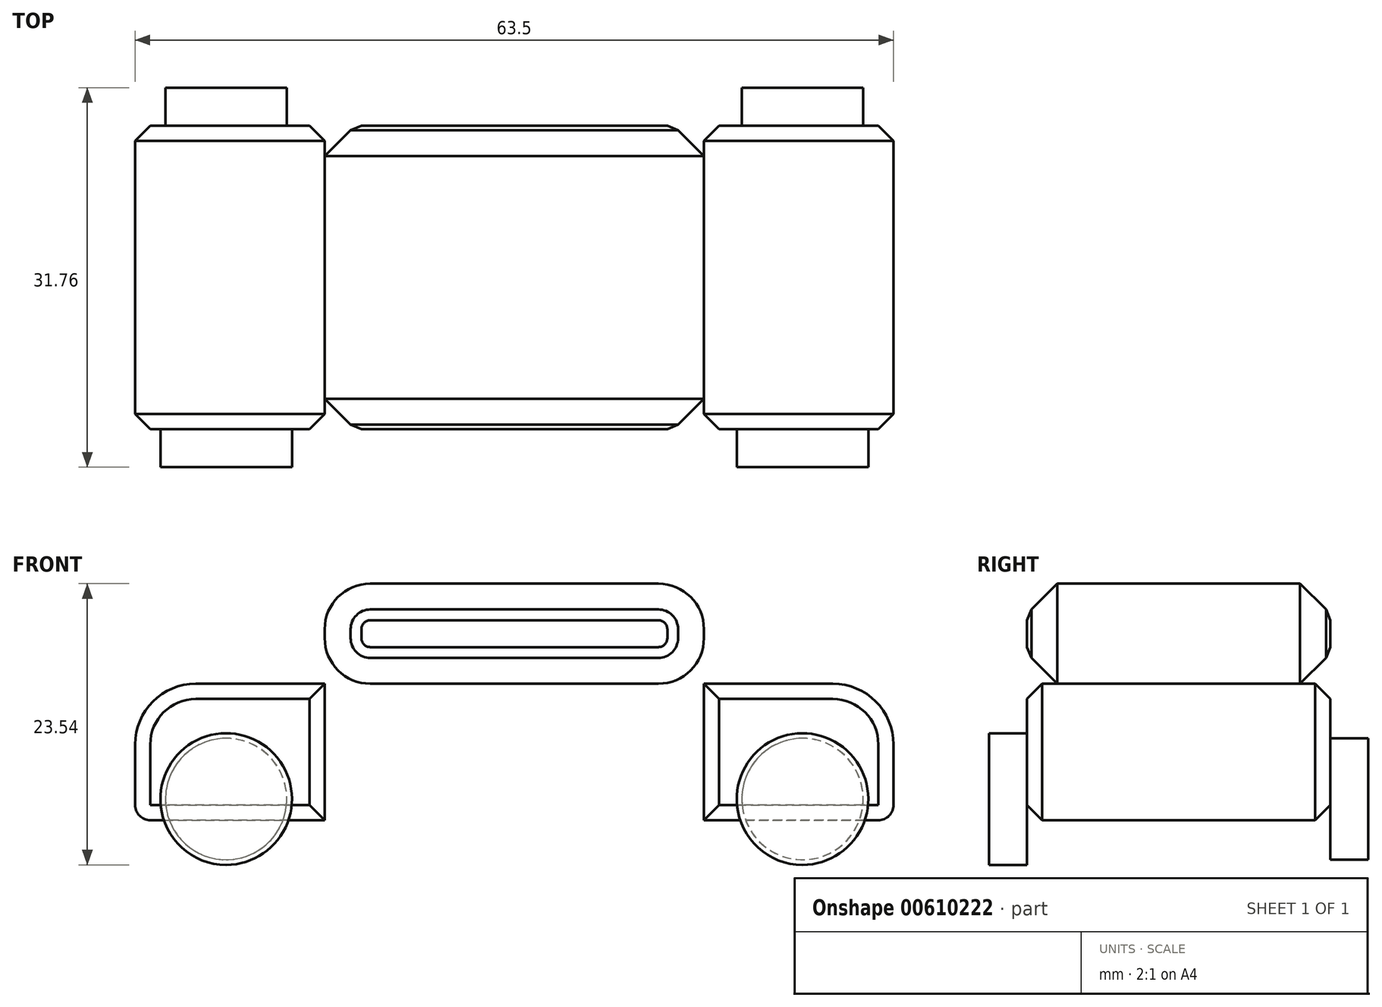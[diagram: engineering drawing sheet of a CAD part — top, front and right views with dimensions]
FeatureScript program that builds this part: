
annotation { "Feature Type Name" : "Feature", "Feature Type Description" : "" }
export const myFeature = defineFeature(function(context is Context, id is Id, definition is map)
    precondition{}
    {
        {
            var Q0;
            Q0=qCreatedBy(makeId("Top.planeOp"),FACE);
            var sketch = newSketch(context, id + "F0", { "sketchPlane" : qUnion([Q0])});
            skLineSegment(sketch, "E0.bottom", {"start": v(0, 0) * mm, "end": v(63.5, 0) * mm});
            skLineSegment(sketch, "E0.top", {"start": v(0, 25.4) * mm, "end": v(63.5, 25.4) * mm});
            skLineSegment(sketch, "E0.left", {"start": v(0, 0) * mm, "end": v(0, 25.4) * mm});
            skLineSegment(sketch, "E0.right", {"start": v(63.5, 0) * mm, "end": v(63.5, 25.4) * mm});
            skLineSegment(sketch, "E1.bottom", {"start": v(47.62, 0) * mm, "end": v(15.88, 0) * mm});
            skLineSegment(sketch, "E1.top", {"start": v(47.62, 25.4) * mm, "end": v(15.88, 25.4) * mm});
            skLineSegment(sketch, "E1.left", {"start": v(47.62, 0) * mm, "end": v(47.62, 25.4) * mm});
            skLineSegment(sketch, "E1.right", {"start": v(15.88, 0) * mm, "end": v(15.88, 25.4) * mm});
            skPoint(sketch, "E1.middle", {"position": v(31.75, 12.7) * mm});
            skSolve(sketch);
        }
        {
            var Q0;
            Q0=makeQuery(id+"F0.imprint","IMPRINT",FACE,{"disambiguationData":[TD([[makeQuery(id+"F0.imprint","IMPRINT",EDGE,{"derivedFrom":sQuery(id+"F0.wireOp",EDGE,"E1.bottom")}),-1.0]])]});
            var Q1;
            {var subQ0=sQuery(id+"F0.wireOp",EDGE,"E0.left");Q1=makeQuery(id+"F0.imprint","IMPRINT",FACE,{"disambiguationData":[TD([[makeQuery(id+"F0.imprint","IMPRINT",EDGE,{"derivedFrom":subQ0}),-1.0]])]});}
            var Q2;
            {var subQ0=sQuery(id+"F0.wireOp",EDGE,"E0.right");Q2=makeQuery(id+"F0.imprint","IMPRINT",FACE,{"disambiguationData":[TD([[makeQuery(id+"F0.imprint","IMPRINT",EDGE,{"derivedFrom":subQ0}),1.0]])]});}
            extrude(context, id + "F1", {"entities" : qUnion([Q0, Q1, Q2]), "depth" : 11.43 * mm, "offsetDistance" : 25.4 * mm});
        }
        {
            var Q0;
            Q0=makeQuery(id+"F1.opExtrude","CAP_FACE",FACE,{"disambiguationData":[OSD([sQuery(id+"F0.wireOp",EDGE,"E0.bottom"),sQuery(id+"F0.wireOp",EDGE,"E0.top"),sQuery(id+"F0.wireOp",EDGE,"E0.left"),sQuery(id+"F0.wireOp",EDGE,"E0.right"),sQuery(id+"F0.wireOp",EDGE,"E1.bottom"),sQuery(id+"F0.wireOp",EDGE,"E1.top")])],"isStart":false});
            var sketch = newSketch(context, id + "F2", { "sketchPlane" : qUnion([Q0])});
            skLineSegment(sketch, "E2.bottom", {"start": v(47.62, 0) * mm, "end": v(15.88, 0) * mm});
            skLineSegment(sketch, "E2.top", {"start": v(47.62, 25.4) * mm, "end": v(15.88, 25.4) * mm});
            skLineSegment(sketch, "E2.left", {"start": v(47.62, 0) * mm, "end": v(47.62, 25.4) * mm});
            skLineSegment(sketch, "E2.right", {"start": v(15.88, 0) * mm, "end": v(15.88, 25.4) * mm});
            skSolve(sketch);
        }
        {
            var Q0;
            Q0 = qSketchRegion(id + "F2", true);
            extrude(context, id + "F3", {"entities" : qUnion([Q0]), "operationType" : NewBodyOperationType.ADD, "depth" : 8.38 * mm, "offsetDistance" : 25.4 * mm});
        }
        {
            var Q0;
            Q0=makeQuery(id+"F3.opExtrude","CAP_EDGE",EDGE,{"disambiguationData":[OSD([sQuery(id+"F2.wireOp",EDGE,"E2.right")])],"isStart":true});
            var Q1;
            Q1=makeQuery(id+"F3.opExtrude","CAP_EDGE",EDGE,{"disambiguationData":[OSD([sQuery(id+"F2.wireOp",EDGE,"E2.left")])],"isStart":true});
            var Q2;
            Q2=makeQuery(id+"F3.opExtrude","CAP_EDGE",EDGE,{"disambiguationData":[OSD([sQuery(id+"F2.wireOp",EDGE,"E2.left")])],"isStart":false});
            var Q3;
            Q3=makeQuery(id+"F3.opExtrude","CAP_EDGE",EDGE,{"disambiguationData":[OSD([sQuery(id+"F2.wireOp",EDGE,"E2.right")])],"isStart":false});
            fillet(context, id + "F4", {"entities" : qUnion([Q0, Q1, Q2, Q3]), "radius" : 3.8 * mm, "tangentPropagation" : true, "allowEdgeOverflow" : false});
        }
        {
            var Q0;
            Q0=makeQuery(id+"F1.opExtrude","CAP_EDGE",EDGE,{"disambiguationData":[OSD([sQuery(id+"F0.wireOp",EDGE,"E0.right")])],"isStart":false});
            var Q1;
            Q1=makeQuery(id+"F1.opExtrude","CAP_EDGE",EDGE,{"disambiguationData":[OSD([sQuery(id+"F0.wireOp",EDGE,"E0.left")])],"isStart":false});
            fillet(context, id + "F5", {"entities" : qUnion([Q0, Q1]), "radius" : 5.08 * mm, "tangentPropagation" : true, "allowEdgeOverflow" : false});
        }
        {
            var Q0;
            Q0=makeQuery(id+"F1.opExtrude","CAP_EDGE",EDGE,{"disambiguationData":[OSD([sQuery(id+"F0.wireOp",EDGE,"E0.right")])],"isStart":true});
            var Q1;
            Q1=makeQuery(id+"F1.opExtrude","CAP_EDGE",EDGE,{"disambiguationData":[OSD([sQuery(id+"F0.wireOp",EDGE,"E0.left")])],"isStart":true});
            fillet(context, id + "F6", {"entities" : qUnion([Q0, Q1]), "radius" : 1.27 * mm, "tangentPropagation" : true, "allowEdgeOverflow" : false});
        }
        {
            var Q0;
            Q0=makeQuery(id+"F5.opFillet","BLEND_EDGE",EDGE,{"blendedFrom":[makeQuery(id+"F1.opExtrude","CAP_EDGE",EDGE,{"disambiguationData":[OSD([sQuery(id+"F0.wireOp",EDGE,"E0.right")])],"isStart":false}),makeQuery(id+"F3.boolean.opBoolean","MERGE",FACE,{"derivedFrom":[makeQuery(id+"F1.opExtrude","SWEPT_FACE",FACE,{"disambiguationData":[OSD([sQuery(id+"F0.wireOp",EDGE,"E0.top"),sQuery(id+"F0.wireOp",EDGE,"E1.top")])]}),makeQuery(id+"F3.opExtrude","SWEPT_FACE",FACE,{"disambiguationData":[OSD([sQuery(id+"F2.wireOp",EDGE,"E2.top")])]})]})],"blendedInto":[makeQuery(id+"F3.boolean.opBoolean","MERGE",FACE,{"derivedFrom":[makeQuery(id+"F1.opExtrude","SWEPT_FACE",FACE,{"disambiguationData":[OSD([sQuery(id+"F0.wireOp",EDGE,"E0.top"),sQuery(id+"F0.wireOp",EDGE,"E1.top")])]}),makeQuery(id+"F3.opExtrude","SWEPT_FACE",FACE,{"disambiguationData":[OSD([sQuery(id+"F2.wireOp",EDGE,"E2.top")])]})]})]});
            var Q1;
            Q1=makeQuery(id+"F1.opExtrude","SWEPT_EDGE",EDGE,{"disambiguationData":[OSD([sQuery(id+"F0.wireOp",EDGE,"E0.top"),sQuery(id+"F0.wireOp",EDGE,"E0.right")])]});
            var Q2;
            Q2=makeQuery(id+"F6.opFillet","BLEND_EDGE",EDGE,{"blendedFrom":[makeQuery(id+"F1.opExtrude","CAP_EDGE",EDGE,{"disambiguationData":[OSD([sQuery(id+"F0.wireOp",EDGE,"E0.right")])],"isStart":true}),makeQuery(id+"F3.boolean.opBoolean","MERGE",FACE,{"derivedFrom":[makeQuery(id+"F1.opExtrude","SWEPT_FACE",FACE,{"disambiguationData":[OSD([sQuery(id+"F0.wireOp",EDGE,"E0.top"),sQuery(id+"F0.wireOp",EDGE,"E1.top")])]}),makeQuery(id+"F3.opExtrude","SWEPT_FACE",FACE,{"disambiguationData":[OSD([sQuery(id+"F2.wireOp",EDGE,"E2.top")])]})]})],"blendedInto":[makeQuery(id+"F3.boolean.opBoolean","MERGE",FACE,{"derivedFrom":[makeQuery(id+"F1.opExtrude","SWEPT_FACE",FACE,{"disambiguationData":[OSD([sQuery(id+"F0.wireOp",EDGE,"E0.top"),sQuery(id+"F0.wireOp",EDGE,"E1.top")])]}),makeQuery(id+"F3.opExtrude","SWEPT_FACE",FACE,{"disambiguationData":[OSD([sQuery(id+"F2.wireOp",EDGE,"E2.top")])]})]})]});
            var Q3;
            Q3=makeQuery(id+"F1.opExtrude","CAP_EDGE",EDGE,{"disambiguationData":[OSD([sQuery(id+"F0.wireOp",EDGE,"E0.top"),sQuery(id+"F0.wireOp",EDGE,"E1.top")])],"isStart":true});
            var Q4;
            {var subQ0=sQuery(id+"F0.wireOp",EDGE,"E0.right");var subQ1=sQuery(id+"F0.wireOp",EDGE,"E1.top");var subQ2=sQuery(id+"F0.wireOp",EDGE,"E0.top");Q4=makeQuery(id+"F3.boolean.opBoolean","SPLIT",EDGE,{"disambiguationData":[TD([makeQuery(id+"F1.opExtrude","SWEPT_FACE",FACE,{"disambiguationData":[OSD([subQ0])]})])],"derivedFrom":makeQuery(id+"F1.opExtrude","CAP_EDGE",EDGE,{"disambiguationData":[OSD([subQ2,subQ1])],"isStart":false})});}
            var Q5;
            Q5=makeQuery(id+"F4.opFillet","BLEND_EDGE",EDGE,{"blendedFrom":[makeQuery(id+"F3.opExtrude","CAP_EDGE",EDGE,{"disambiguationData":[OSD([sQuery(id+"F2.wireOp",EDGE,"E2.left")])],"isStart":true}),makeQuery(id+"F3.boolean.opBoolean","MERGE",FACE,{"derivedFrom":[makeQuery(id+"F1.opExtrude","SWEPT_FACE",FACE,{"disambiguationData":[OSD([sQuery(id+"F0.wireOp",EDGE,"E0.top"),sQuery(id+"F0.wireOp",EDGE,"E1.top")])]}),makeQuery(id+"F3.opExtrude","SWEPT_FACE",FACE,{"disambiguationData":[OSD([sQuery(id+"F2.wireOp",EDGE,"E2.top")])]})]})],"blendedInto":[makeQuery(id+"F3.boolean.opBoolean","MERGE",FACE,{"derivedFrom":[makeQuery(id+"F1.opExtrude","SWEPT_FACE",FACE,{"disambiguationData":[OSD([sQuery(id+"F0.wireOp",EDGE,"E0.top"),sQuery(id+"F0.wireOp",EDGE,"E1.top")])]}),makeQuery(id+"F3.opExtrude","SWEPT_FACE",FACE,{"disambiguationData":[OSD([sQuery(id+"F2.wireOp",EDGE,"E2.top")])]})]})]});
            var Q6;
            Q6=makeQuery(id+"F4.opFillet","BLEND_EDGE",EDGE,{"blendedFrom":[makeQuery(id+"F3.opExtrude","CAP_EDGE",EDGE,{"disambiguationData":[OSD([sQuery(id+"F2.wireOp",EDGE,"E2.left")])],"isStart":false}),makeQuery(id+"F3.boolean.opBoolean","MERGE",FACE,{"derivedFrom":[makeQuery(id+"F1.opExtrude","SWEPT_FACE",FACE,{"disambiguationData":[OSD([sQuery(id+"F0.wireOp",EDGE,"E0.top"),sQuery(id+"F0.wireOp",EDGE,"E1.top")])]}),makeQuery(id+"F3.opExtrude","SWEPT_FACE",FACE,{"disambiguationData":[OSD([sQuery(id+"F2.wireOp",EDGE,"E2.top")])]})]})],"blendedInto":[makeQuery(id+"F3.boolean.opBoolean","MERGE",FACE,{"derivedFrom":[makeQuery(id+"F1.opExtrude","SWEPT_FACE",FACE,{"disambiguationData":[OSD([sQuery(id+"F0.wireOp",EDGE,"E0.top"),sQuery(id+"F0.wireOp",EDGE,"E1.top")])]}),makeQuery(id+"F3.opExtrude","SWEPT_FACE",FACE,{"disambiguationData":[OSD([sQuery(id+"F2.wireOp",EDGE,"E2.top")])]})]})]});
            var Q7;
            Q7=makeQuery(id+"F3.opExtrude","CAP_EDGE",EDGE,{"disambiguationData":[OSD([sQuery(id+"F2.wireOp",EDGE,"E2.top")])],"isStart":false});
            var Q8;
            Q8=makeQuery(id+"F4.opFillet","BLEND_EDGE",EDGE,{"blendedFrom":[makeQuery(id+"F3.opExtrude","CAP_EDGE",EDGE,{"disambiguationData":[OSD([sQuery(id+"F2.wireOp",EDGE,"E2.right")])],"isStart":false}),makeQuery(id+"F3.boolean.opBoolean","MERGE",FACE,{"derivedFrom":[makeQuery(id+"F1.opExtrude","SWEPT_FACE",FACE,{"disambiguationData":[OSD([sQuery(id+"F0.wireOp",EDGE,"E0.top"),sQuery(id+"F0.wireOp",EDGE,"E1.top")])]}),makeQuery(id+"F3.opExtrude","SWEPT_FACE",FACE,{"disambiguationData":[OSD([sQuery(id+"F2.wireOp",EDGE,"E2.top")])]})]})],"blendedInto":[makeQuery(id+"F3.boolean.opBoolean","MERGE",FACE,{"derivedFrom":[makeQuery(id+"F1.opExtrude","SWEPT_FACE",FACE,{"disambiguationData":[OSD([sQuery(id+"F0.wireOp",EDGE,"E0.top"),sQuery(id+"F0.wireOp",EDGE,"E1.top")])]}),makeQuery(id+"F3.opExtrude","SWEPT_FACE",FACE,{"disambiguationData":[OSD([sQuery(id+"F2.wireOp",EDGE,"E2.top")])]})]})]});
            var Q9;
            Q9=makeQuery(id+"F4.opFillet","BLEND_EDGE",EDGE,{"blendedFrom":[makeQuery(id+"F3.opExtrude","CAP_EDGE",EDGE,{"disambiguationData":[OSD([sQuery(id+"F2.wireOp",EDGE,"E2.right")])],"isStart":true}),makeQuery(id+"F3.boolean.opBoolean","MERGE",FACE,{"derivedFrom":[makeQuery(id+"F1.opExtrude","SWEPT_FACE",FACE,{"disambiguationData":[OSD([sQuery(id+"F0.wireOp",EDGE,"E0.top"),sQuery(id+"F0.wireOp",EDGE,"E1.top")])]}),makeQuery(id+"F3.opExtrude","SWEPT_FACE",FACE,{"disambiguationData":[OSD([sQuery(id+"F2.wireOp",EDGE,"E2.top")])]})]})],"blendedInto":[makeQuery(id+"F3.boolean.opBoolean","MERGE",FACE,{"derivedFrom":[makeQuery(id+"F1.opExtrude","SWEPT_FACE",FACE,{"disambiguationData":[OSD([sQuery(id+"F0.wireOp",EDGE,"E0.top"),sQuery(id+"F0.wireOp",EDGE,"E1.top")])]}),makeQuery(id+"F3.opExtrude","SWEPT_FACE",FACE,{"disambiguationData":[OSD([sQuery(id+"F2.wireOp",EDGE,"E2.top")])]})]})]});
            var Q10;
            {var subQ0=sQuery(id+"F0.wireOp",EDGE,"E0.left");var subQ1=sQuery(id+"F0.wireOp",EDGE,"E1.top");var subQ2=sQuery(id+"F0.wireOp",EDGE,"E0.top");Q10=makeQuery(id+"F3.boolean.opBoolean","SPLIT",EDGE,{"disambiguationData":[TD([makeQuery(id+"F1.opExtrude","SWEPT_FACE",FACE,{"disambiguationData":[OSD([subQ0])]})])],"derivedFrom":makeQuery(id+"F1.opExtrude","CAP_EDGE",EDGE,{"disambiguationData":[OSD([subQ2,subQ1])],"isStart":false})});}
            var Q11;
            Q11=makeQuery(id+"F5.opFillet","BLEND_EDGE",EDGE,{"blendedFrom":[makeQuery(id+"F1.opExtrude","CAP_EDGE",EDGE,{"disambiguationData":[OSD([sQuery(id+"F0.wireOp",EDGE,"E0.left")])],"isStart":false}),makeQuery(id+"F3.boolean.opBoolean","MERGE",FACE,{"derivedFrom":[makeQuery(id+"F1.opExtrude","SWEPT_FACE",FACE,{"disambiguationData":[OSD([sQuery(id+"F0.wireOp",EDGE,"E0.top"),sQuery(id+"F0.wireOp",EDGE,"E1.top")])]}),makeQuery(id+"F3.opExtrude","SWEPT_FACE",FACE,{"disambiguationData":[OSD([sQuery(id+"F2.wireOp",EDGE,"E2.top")])]})]})],"blendedInto":[makeQuery(id+"F3.boolean.opBoolean","MERGE",FACE,{"derivedFrom":[makeQuery(id+"F1.opExtrude","SWEPT_FACE",FACE,{"disambiguationData":[OSD([sQuery(id+"F0.wireOp",EDGE,"E0.top"),sQuery(id+"F0.wireOp",EDGE,"E1.top")])]}),makeQuery(id+"F3.opExtrude","SWEPT_FACE",FACE,{"disambiguationData":[OSD([sQuery(id+"F2.wireOp",EDGE,"E2.top")])]})]})]});
            var Q12;
            Q12=makeQuery(id+"F1.opExtrude","SWEPT_EDGE",EDGE,{"disambiguationData":[OSD([sQuery(id+"F0.wireOp",EDGE,"E0.top"),sQuery(id+"F0.wireOp",EDGE,"E0.left")])]});
            var Q13;
            Q13=makeQuery(id+"F6.opFillet","BLEND_EDGE",EDGE,{"blendedFrom":[makeQuery(id+"F1.opExtrude","CAP_EDGE",EDGE,{"disambiguationData":[OSD([sQuery(id+"F0.wireOp",EDGE,"E0.left")])],"isStart":true}),makeQuery(id+"F3.boolean.opBoolean","MERGE",FACE,{"derivedFrom":[makeQuery(id+"F1.opExtrude","SWEPT_FACE",FACE,{"disambiguationData":[OSD([sQuery(id+"F0.wireOp",EDGE,"E0.top"),sQuery(id+"F0.wireOp",EDGE,"E1.top")])]}),makeQuery(id+"F3.opExtrude","SWEPT_FACE",FACE,{"disambiguationData":[OSD([sQuery(id+"F2.wireOp",EDGE,"E2.top")])]})]})],"blendedInto":[makeQuery(id+"F3.boolean.opBoolean","MERGE",FACE,{"derivedFrom":[makeQuery(id+"F1.opExtrude","SWEPT_FACE",FACE,{"disambiguationData":[OSD([sQuery(id+"F0.wireOp",EDGE,"E0.top"),sQuery(id+"F0.wireOp",EDGE,"E1.top")])]}),makeQuery(id+"F3.opExtrude","SWEPT_FACE",FACE,{"disambiguationData":[OSD([sQuery(id+"F2.wireOp",EDGE,"E2.top")])]})]})]});
            var Q14;
            Q14=makeQuery(id+"F1.opExtrude","CAP_EDGE",EDGE,{"disambiguationData":[OSD([sQuery(id+"F0.wireOp",EDGE,"E0.bottom"),sQuery(id+"F0.wireOp",EDGE,"E1.bottom")])],"isStart":true});
            var Q15;
            Q15=makeQuery(id+"F1.opExtrude","SWEPT_EDGE",EDGE,{"disambiguationData":[OSD([sQuery(id+"F0.wireOp",EDGE,"E0.bottom"),sQuery(id+"F0.wireOp",EDGE,"E0.left")])]});
            var Q16;
            Q16=makeQuery(id+"F5.opFillet","BLEND_EDGE",EDGE,{"blendedFrom":[makeQuery(id+"F1.opExtrude","CAP_EDGE",EDGE,{"disambiguationData":[OSD([sQuery(id+"F0.wireOp",EDGE,"E0.left")])],"isStart":false}),makeQuery(id+"F3.boolean.opBoolean","MERGE",FACE,{"derivedFrom":[makeQuery(id+"F1.opExtrude","SWEPT_FACE",FACE,{"disambiguationData":[OSD([sQuery(id+"F0.wireOp",EDGE,"E0.bottom"),sQuery(id+"F0.wireOp",EDGE,"E1.bottom")])]}),makeQuery(id+"F3.opExtrude","SWEPT_FACE",FACE,{"disambiguationData":[OSD([sQuery(id+"F2.wireOp",EDGE,"E2.bottom")])]})]})],"blendedInto":[makeQuery(id+"F3.boolean.opBoolean","MERGE",FACE,{"derivedFrom":[makeQuery(id+"F1.opExtrude","SWEPT_FACE",FACE,{"disambiguationData":[OSD([sQuery(id+"F0.wireOp",EDGE,"E0.bottom"),sQuery(id+"F0.wireOp",EDGE,"E1.bottom")])]}),makeQuery(id+"F3.opExtrude","SWEPT_FACE",FACE,{"disambiguationData":[OSD([sQuery(id+"F2.wireOp",EDGE,"E2.bottom")])]})]})]});
            var Q17;
            {var subQ0=sQuery(id+"F0.wireOp",EDGE,"E1.bottom");var subQ1=sQuery(id+"F0.wireOp",EDGE,"E0.left");var subQ2=sQuery(id+"F0.wireOp",EDGE,"E0.bottom");Q17=makeQuery(id+"F3.boolean.opBoolean","SPLIT",EDGE,{"disambiguationData":[TD([makeQuery(id+"F1.opExtrude","SWEPT_FACE",FACE,{"disambiguationData":[OSD([subQ1])]})])],"derivedFrom":makeQuery(id+"F1.opExtrude","CAP_EDGE",EDGE,{"disambiguationData":[OSD([subQ2,subQ0])],"isStart":false})});}
            var Q18;
            Q18=makeQuery(id+"F4.opFillet","BLEND_EDGE",EDGE,{"blendedFrom":[makeQuery(id+"F3.opExtrude","CAP_EDGE",EDGE,{"disambiguationData":[OSD([sQuery(id+"F2.wireOp",EDGE,"E2.right")])],"isStart":true}),makeQuery(id+"F3.boolean.opBoolean","MERGE",FACE,{"derivedFrom":[makeQuery(id+"F1.opExtrude","SWEPT_FACE",FACE,{"disambiguationData":[OSD([sQuery(id+"F0.wireOp",EDGE,"E0.bottom"),sQuery(id+"F0.wireOp",EDGE,"E1.bottom")])]}),makeQuery(id+"F3.opExtrude","SWEPT_FACE",FACE,{"disambiguationData":[OSD([sQuery(id+"F2.wireOp",EDGE,"E2.bottom")])]})]})],"blendedInto":[makeQuery(id+"F3.boolean.opBoolean","MERGE",FACE,{"derivedFrom":[makeQuery(id+"F1.opExtrude","SWEPT_FACE",FACE,{"disambiguationData":[OSD([sQuery(id+"F0.wireOp",EDGE,"E0.bottom"),sQuery(id+"F0.wireOp",EDGE,"E1.bottom")])]}),makeQuery(id+"F3.opExtrude","SWEPT_FACE",FACE,{"disambiguationData":[OSD([sQuery(id+"F2.wireOp",EDGE,"E2.bottom")])]})]})]});
            var Q19;
            Q19=makeQuery(id+"F4.opFillet","BLEND_EDGE",EDGE,{"blendedFrom":[makeQuery(id+"F3.opExtrude","CAP_EDGE",EDGE,{"disambiguationData":[OSD([sQuery(id+"F2.wireOp",EDGE,"E2.right")])],"isStart":false}),makeQuery(id+"F3.boolean.opBoolean","MERGE",FACE,{"derivedFrom":[makeQuery(id+"F1.opExtrude","SWEPT_FACE",FACE,{"disambiguationData":[OSD([sQuery(id+"F0.wireOp",EDGE,"E0.bottom"),sQuery(id+"F0.wireOp",EDGE,"E1.bottom")])]}),makeQuery(id+"F3.opExtrude","SWEPT_FACE",FACE,{"disambiguationData":[OSD([sQuery(id+"F2.wireOp",EDGE,"E2.bottom")])]})]})],"blendedInto":[makeQuery(id+"F3.boolean.opBoolean","MERGE",FACE,{"derivedFrom":[makeQuery(id+"F1.opExtrude","SWEPT_FACE",FACE,{"disambiguationData":[OSD([sQuery(id+"F0.wireOp",EDGE,"E0.bottom"),sQuery(id+"F0.wireOp",EDGE,"E1.bottom")])]}),makeQuery(id+"F3.opExtrude","SWEPT_FACE",FACE,{"disambiguationData":[OSD([sQuery(id+"F2.wireOp",EDGE,"E2.bottom")])]})]})]});
            var Q20;
            Q20=makeQuery(id+"F3.opExtrude","CAP_EDGE",EDGE,{"disambiguationData":[OSD([sQuery(id+"F2.wireOp",EDGE,"E2.bottom")])],"isStart":false});
            var Q21;
            Q21=makeQuery(id+"F3.opExtrude","SWEPT_EDGE",EDGE,{"disambiguationData":[OSD([sQuery(id+"F0.wireOp",EDGE,"E0.bottom"),sQuery(id+"F0.wireOp",EDGE,"E1.bottom"),sQuery(id+"F2.wireOp",EDGE,"E2.bottom"),sQuery(id+"F2.wireOp",EDGE,"E2.right")])]});
            var Q22;
            Q22=makeQuery(id+"F3.opExtrude","SWEPT_EDGE",EDGE,{"disambiguationData":[OSD([sQuery(id+"F0.wireOp",EDGE,"E0.top"),sQuery(id+"F0.wireOp",EDGE,"E1.top"),sQuery(id+"F2.wireOp",EDGE,"E2.top"),sQuery(id+"F2.wireOp",EDGE,"E2.right")])]});
            var Q23;
            Q23=makeQuery(id+"F1.opExtrude","SWEPT_EDGE",EDGE,{"disambiguationData":[OSD([sQuery(id+"F0.wireOp",EDGE,"E0.bottom"),sQuery(id+"F0.wireOp",EDGE,"E0.right")])]});
            var Q24;
            Q24=makeQuery(id+"F5.opFillet","BLEND_EDGE",EDGE,{"blendedFrom":[makeQuery(id+"F1.opExtrude","CAP_EDGE",EDGE,{"disambiguationData":[OSD([sQuery(id+"F0.wireOp",EDGE,"E0.right")])],"isStart":false}),makeQuery(id+"F3.boolean.opBoolean","MERGE",FACE,{"derivedFrom":[makeQuery(id+"F1.opExtrude","SWEPT_FACE",FACE,{"disambiguationData":[OSD([sQuery(id+"F0.wireOp",EDGE,"E0.bottom"),sQuery(id+"F0.wireOp",EDGE,"E1.bottom")])]}),makeQuery(id+"F3.opExtrude","SWEPT_FACE",FACE,{"disambiguationData":[OSD([sQuery(id+"F2.wireOp",EDGE,"E2.bottom")])]})]})],"blendedInto":[makeQuery(id+"F3.boolean.opBoolean","MERGE",FACE,{"derivedFrom":[makeQuery(id+"F1.opExtrude","SWEPT_FACE",FACE,{"disambiguationData":[OSD([sQuery(id+"F0.wireOp",EDGE,"E0.bottom"),sQuery(id+"F0.wireOp",EDGE,"E1.bottom")])]}),makeQuery(id+"F3.opExtrude","SWEPT_FACE",FACE,{"disambiguationData":[OSD([sQuery(id+"F2.wireOp",EDGE,"E2.bottom")])]})]})]});
            var Q25;
            {var subQ0=sQuery(id+"F0.wireOp",EDGE,"E1.bottom");var subQ1=sQuery(id+"F0.wireOp",EDGE,"E0.right");var subQ2=sQuery(id+"F0.wireOp",EDGE,"E0.bottom");Q25=makeQuery(id+"F3.boolean.opBoolean","SPLIT",EDGE,{"disambiguationData":[TD([makeQuery(id+"F1.opExtrude","SWEPT_FACE",FACE,{"disambiguationData":[OSD([subQ1])]})])],"derivedFrom":makeQuery(id+"F1.opExtrude","CAP_EDGE",EDGE,{"disambiguationData":[OSD([subQ2,subQ0])],"isStart":false})});}
            var Q26;
            Q26=makeQuery(id+"F4.opFillet","BLEND_EDGE",EDGE,{"blendedFrom":[makeQuery(id+"F3.opExtrude","CAP_EDGE",EDGE,{"disambiguationData":[OSD([sQuery(id+"F2.wireOp",EDGE,"E2.left")])],"isStart":true}),makeQuery(id+"F3.boolean.opBoolean","MERGE",FACE,{"derivedFrom":[makeQuery(id+"F1.opExtrude","SWEPT_FACE",FACE,{"disambiguationData":[OSD([sQuery(id+"F0.wireOp",EDGE,"E0.bottom"),sQuery(id+"F0.wireOp",EDGE,"E1.bottom")])]}),makeQuery(id+"F3.opExtrude","SWEPT_FACE",FACE,{"disambiguationData":[OSD([sQuery(id+"F2.wireOp",EDGE,"E2.bottom")])]})]})],"blendedInto":[makeQuery(id+"F3.boolean.opBoolean","MERGE",FACE,{"derivedFrom":[makeQuery(id+"F1.opExtrude","SWEPT_FACE",FACE,{"disambiguationData":[OSD([sQuery(id+"F0.wireOp",EDGE,"E0.bottom"),sQuery(id+"F0.wireOp",EDGE,"E1.bottom")])]}),makeQuery(id+"F3.opExtrude","SWEPT_FACE",FACE,{"disambiguationData":[OSD([sQuery(id+"F2.wireOp",EDGE,"E2.bottom")])]})]})]});
            var Q27;
            Q27=makeQuery(id+"F4.opFillet","BLEND_EDGE",EDGE,{"blendedFrom":[makeQuery(id+"F3.opExtrude","CAP_EDGE",EDGE,{"disambiguationData":[OSD([sQuery(id+"F2.wireOp",EDGE,"E2.left")])],"isStart":false}),makeQuery(id+"F3.boolean.opBoolean","MERGE",FACE,{"derivedFrom":[makeQuery(id+"F1.opExtrude","SWEPT_FACE",FACE,{"disambiguationData":[OSD([sQuery(id+"F0.wireOp",EDGE,"E0.bottom"),sQuery(id+"F0.wireOp",EDGE,"E1.bottom")])]}),makeQuery(id+"F3.opExtrude","SWEPT_FACE",FACE,{"disambiguationData":[OSD([sQuery(id+"F2.wireOp",EDGE,"E2.bottom")])]})]})],"blendedInto":[makeQuery(id+"F3.boolean.opBoolean","MERGE",FACE,{"derivedFrom":[makeQuery(id+"F1.opExtrude","SWEPT_FACE",FACE,{"disambiguationData":[OSD([sQuery(id+"F0.wireOp",EDGE,"E0.bottom"),sQuery(id+"F0.wireOp",EDGE,"E1.bottom")])]}),makeQuery(id+"F3.opExtrude","SWEPT_FACE",FACE,{"disambiguationData":[OSD([sQuery(id+"F2.wireOp",EDGE,"E2.bottom")])]})]})]});
            var Q28;
            Q28=makeQuery(id+"F3.opExtrude","SWEPT_EDGE",EDGE,{"disambiguationData":[OSD([sQuery(id+"F0.wireOp",EDGE,"E0.bottom"),sQuery(id+"F0.wireOp",EDGE,"E1.bottom"),sQuery(id+"F2.wireOp",EDGE,"E2.bottom"),sQuery(id+"F2.wireOp",EDGE,"E2.left")])]});
            var Q29;
            Q29=makeQuery(id+"F3.opExtrude","SWEPT_EDGE",EDGE,{"disambiguationData":[OSD([sQuery(id+"F0.wireOp",EDGE,"E0.top"),sQuery(id+"F0.wireOp",EDGE,"E1.top"),sQuery(id+"F2.wireOp",EDGE,"E2.top"),sQuery(id+"F2.wireOp",EDGE,"E2.left")])]});
            chamfer(context, id + "F7", {"entities" : qUnion([Q0, Q1, Q2, Q3, Q4, Q5, Q6, Q7, Q8, Q9, Q10, Q11, Q12, Q13, Q14, Q15, Q16, Q17, Q18, Q19, Q20, Q21, Q22, Q23, Q24, Q25, Q26, Q27, Q28, Q29]), "width" : 2.54 * mm, "tangentPropagation" : true});
        }
        {
            var Q0;
            Q0=makeQuery(id+"F3.boolean.opBoolean","MERGE",FACE,{"derivedFrom":[makeQuery(id+"F1.opExtrude","SWEPT_FACE",FACE,{"disambiguationData":[OSD([sQuery(id+"F0.wireOp",EDGE,"E0.top"),sQuery(id+"F0.wireOp",EDGE,"E1.top")])]}),makeQuery(id+"F3.opExtrude","SWEPT_FACE",FACE,{"disambiguationData":[OSD([sQuery(id+"F2.wireOp",EDGE,"E2.top")])]})]});
            var Q1;
            Q1=makeQuery(id+"F3.boolean.opBoolean","MERGE",FACE,{"derivedFrom":[makeQuery(id+"F1.opExtrude","SWEPT_FACE",FACE,{"disambiguationData":[OSD([sQuery(id+"F0.wireOp",EDGE,"E0.bottom"),sQuery(id+"F0.wireOp",EDGE,"E1.bottom")])]}),makeQuery(id+"F3.opExtrude","SWEPT_FACE",FACE,{"disambiguationData":[OSD([sQuery(id+"F2.wireOp",EDGE,"E2.bottom")])]})]});
            chamfer(context, id + "F8", {"entities" : qUnion([Q0, Q1]), "width" : 1.27 * mm, "tangentPropagation" : true});
        }
        {
            var Q0;
            Q0=makeQuery(id+"F3.boolean.opBoolean","MERGE",FACE,{"derivedFrom":[makeQuery(id+"F1.opExtrude","SWEPT_FACE",FACE,{"disambiguationData":[OSD([sQuery(id+"F0.wireOp",EDGE,"E0.top"),sQuery(id+"F0.wireOp",EDGE,"E1.top")])]}),makeQuery(id+"F3.opExtrude","SWEPT_FACE",FACE,{"disambiguationData":[OSD([sQuery(id+"F2.wireOp",EDGE,"E2.top")])]})]});
            var sketch = newSketch(context, id + "F9", { "sketchPlane" : qUnion([Q0])});
            skCircle(sketch, "E3", {"center": v(-55.88, 1.78) * mm, "radius": 5.08 * mm});
            skCircle(sketch, "E4.MirrorC", {"center": v(-7.62, 1.78) * mm, "radius": 5.08 * mm});
            skSolve(sketch);
        }
        {
            var Q0;
            Q0 = qSketchRegion(id + "F9", true);
            extrude(context, id + "F10", {"entities" : qUnion([Q0]), "operationType" : NewBodyOperationType.ADD, "depth" : 3.17 * mm, "offsetDistance" : 25.4 * mm});
        }
        {
            var Q0;
            Q0=makeQuery(id+"F3.boolean.opBoolean","MERGE",FACE,{"derivedFrom":[makeQuery(id+"F1.opExtrude","SWEPT_FACE",FACE,{"disambiguationData":[OSD([sQuery(id+"F0.wireOp",EDGE,"E0.bottom"),sQuery(id+"F0.wireOp",EDGE,"E1.bottom")])]}),makeQuery(id+"F3.opExtrude","SWEPT_FACE",FACE,{"disambiguationData":[OSD([sQuery(id+"F2.wireOp",EDGE,"E2.bottom")])]})]});
            var sketch = newSketch(context, id + "F11", { "sketchPlane" : qUnion([Q0])});
            skCircle(sketch, "E5", {"center": v(7.62, 1.78) * mm, "radius": 5.5 * mm});
            skLineSegment(sketch, "E6", {"start": v(31.75, 18.54) * mm, "end": v(31.75, 1.27) * mm});
            skCircle(sketch, "E7.MirrorC", {"center": v(55.88, 1.78) * mm, "radius": 5.5 * mm});
            skSolve(sketch);
        }
        {
            var Q0;
            Q0 = qSketchRegion(id + "F11", true);
            extrude(context, id + "F12", {"entities" : qUnion([Q0]), "operationType" : NewBodyOperationType.ADD, "depth" : 3.17 * mm, "offsetDistance" : 25.4 * mm});
        }
    });
